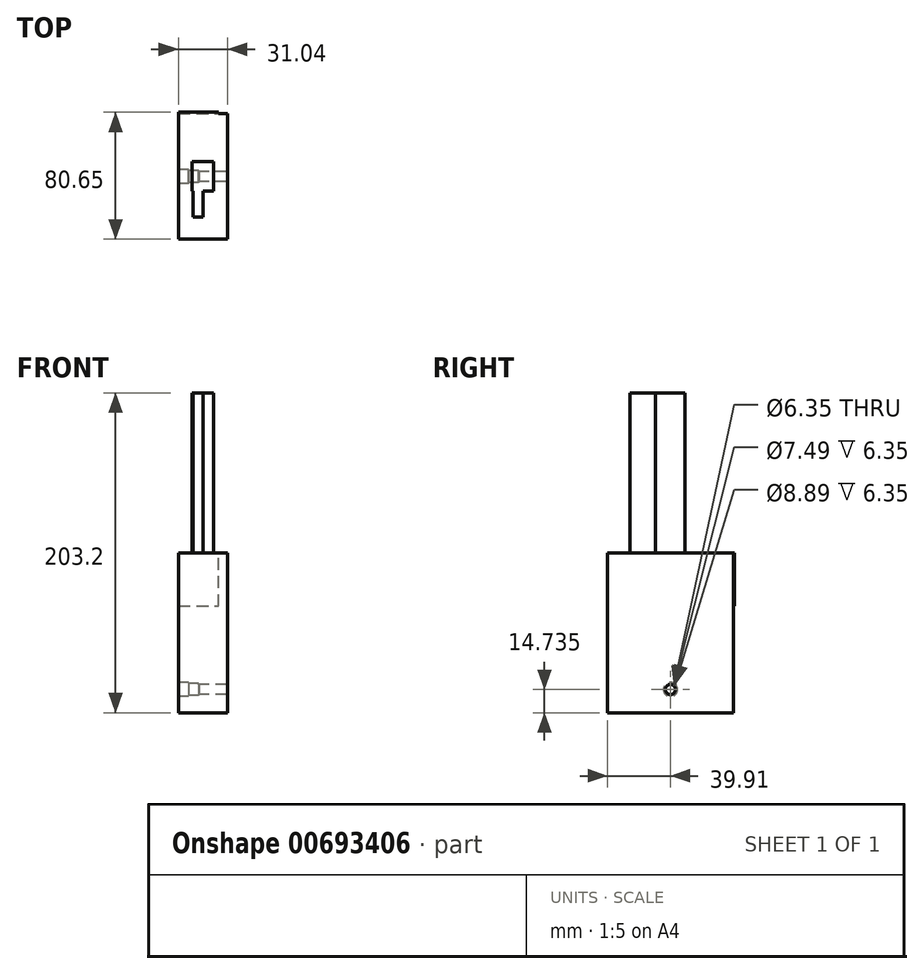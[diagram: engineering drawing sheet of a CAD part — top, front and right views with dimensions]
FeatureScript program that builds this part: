
annotation { "Feature Type Name" : "Feature", "Feature Type Description" : "" }
export const myFeature = defineFeature(function(context is Context, id is Id, definition is map)
    precondition{}
    {
        {
            var Q0;
            Q0=qCreatedBy(makeId("Top.planeOp"),FACE);
            var sketch = newSketch(context, id + "F0", { "sketchPlane" : qUnion([Q0])});
            skLineSegment(sketch, "E0.bottom", {"start": v(-15.52, 39.91) * mm, "end": v(15.52, 39.91) * mm});
            skLineSegment(sketch, "E0.top", {"start": v(-15.52, -39.91) * mm, "end": v(15.52, -39.91) * mm});
            skLineSegment(sketch, "E0.left", {"start": v(-15.52, 39.91) * mm, "end": v(-15.52, -39.91) * mm});
            skLineSegment(sketch, "E0.right", {"start": v(15.52, 39.91) * mm, "end": v(15.52, -39.91) * mm});
            skPoint(sketch, "E0.middle", {"position": v(0, 0) * mm});
            skSolve(sketch);
        }
        {
            var Q0;
            Q0=makeQuery(id+"F0.imprint","IMPRINT",FACE,{"disambiguationData":[TD([[makeQuery(id+"F0.imprint","IMPRINT",EDGE,{"derivedFrom":sQuery(id+"F0.wireOp",EDGE,"E0.bottom")}),-1.0]])]});
            extrude(context, id + "F1", {"entities" : qUnion([Q0]), "depth" : 101.6 * mm, "offsetDistance" : 25.4 * mm});
        }
        {
            var Q0;
            Q0=makeQuery(id+"F1.opExtrude","SWEPT_FACE",FACE,{"disambiguationData":[OSD([sQuery(id+"F0.wireOp",EDGE,"E0.left")])]});
            var sketch = newSketch(context, id + "F2", { "sketchPlane" : qUnion([Q0])});
            skPoint(sketch, "E1", {"position": v(0, 14.73) * mm});
            skSolve(sketch);
        }
        {
            var Q0;
            Q0=sQuery(id+"F2.wireOp",VERTEX,"E1");
            var Q1;
            Q1=makeQuery(id+"F1.opExtrude","SWEPT_BODY",BODY,{"disambiguationData":[OSD([sQuery(id+"F0.wireOp",EDGE,"E0.bottom"),sQuery(id+"F0.wireOp",EDGE,"E0.top"),sQuery(id+"F0.wireOp",EDGE,"E0.left"),sQuery(id+"F0.wireOp",EDGE,"E0.right")])]});
            hole(context, id + "F3", {"style" : HoleStyle.SIMPLE, "endStyle" : HoleEndStyle.THROUGH, "holeDiameter" : 6.35 * mm, "majorDiameter" : 6.35 * mm, "isTappedThrough" : true, "tappedDepth" : 12.7 * mm, "tapClearance" : 3, "locations" : qUnion([Q0]), "scope" : qUnion([Q1])});
        }
        {
            var Q0;
            Q0=makeQuery(id+"F1.opExtrude","SWEPT_FACE",FACE,{"disambiguationData":[OSD([sQuery(id+"F0.wireOp",EDGE,"E0.left")])]});
            var sketch = newSketch(context, id + "F4", { "sketchPlane" : qUnion([Q0])});
            skCircle(sketch, "E2", {"center": v(0, 14.73) * mm, "radius": 5.53 * mm});
            skSolve(sketch);
        }
        {
            var Q0;
            Q0=sQuery(id+"F4.wireOp",VERTEX,"E2.center");
            var Q1;
            Q1=makeQuery(id+"F1.opExtrude","SWEPT_BODY",BODY,{"disambiguationData":[OSD([sQuery(id+"F0.wireOp",EDGE,"E0.bottom"),sQuery(id+"F0.wireOp",EDGE,"E0.top"),sQuery(id+"F0.wireOp",EDGE,"E0.left"),sQuery(id+"F0.wireOp",EDGE,"E0.right")])]});
            hole(context, id + "F5", {"style" : HoleStyle.C_BORE, "endStyle" : HoleEndStyle.BLIND, "holeDiameter" : 7.5 * mm, "cBoreDiameter" : 8.9 * mm, "cBoreDepth" : 6.35 * mm, "majorDiameter" : 6.35 * mm, "holeDepth" : 12.7 * mm, "isTappedThrough" : true, "tappedDepth" : 12.7 * mm, "tapClearance" : 3, "locations" : qUnion([Q0]), "scope" : qUnion([Q1])});
        }
        {
            var Q0;
            Q0=makeQuery(id+"F1.opExtrude","SWEPT_FACE",FACE,{"disambiguationData":[OSD([sQuery(id+"F0.wireOp",EDGE,"E0.left")])]});
            var sketch = newSketch(context, id + "F6", { "sketchPlane" : qUnion([Q0])});
            skLineSegment(sketch, "E3.bottom", {"start": v(6.59, 101.6) * mm, "end": v(-40.74, 101.6) * mm});
            skLineSegment(sketch, "E3.top", {"start": v(6.59, 67.7) * mm, "end": v(-40.74, 67.7) * mm});
            skLineSegment(sketch, "E3.left", {"start": v(6.59, 101.6) * mm, "end": v(6.59, 67.7) * mm});
            skLineSegment(sketch, "E3.right", {"start": v(-40.74, 101.6) * mm, "end": v(-40.74, 67.7) * mm});
            skPoint(sketch, "E3.middle", {"position": v(-17.08, 84.65) * mm});
            skLineSegment(sketch, "E4.bottom", {"start": v(0, 84.65) * mm, "end": v(-34.15, 84.65) * mm});
            skLineSegment(sketch, "E4.top", {"start": v(0, 84.65) * mm, "end": v(-34.15, 84.65) * mm});
            skLineSegment(sketch, "E4.left", {"start": v(0, 84.65) * mm, "end": v(0, 84.65) * mm});
            skLineSegment(sketch, "E4.right", {"start": v(-34.15, 84.65) * mm, "end": v(-34.15, 84.65) * mm});
            skSolve(sketch);
        }
        {
            var Q0;
            Q0 = qSketchRegion(id + "F6", true);
            extrude(context, id + "F7", {"entities" : qUnion([Q0]), "operationType" : NewBodyOperationType.ADD, "oppositeDirection" : true, "depth" : 25.4 * mm, "offsetDistance" : 25.4 * mm});
        }
        {
            var Q0;
            Q0=makeQuery(id+"F7.boolean.opBoolean","MERGE",FACE,{"derivedFrom":[makeQuery(id+"F1.opExtrude","CAP_FACE",FACE,{"disambiguationData":[OSD([sQuery(id+"F0.wireOp",EDGE,"E0.bottom"),sQuery(id+"F0.wireOp",EDGE,"E0.top"),sQuery(id+"F0.wireOp",EDGE,"E0.left"),sQuery(id+"F0.wireOp",EDGE,"E0.right")])],"isStart":false}),makeQuery(id+"F7.opExtrude","SWEPT_FACE",FACE,{"disambiguationData":[OSD([sQuery(id+"F6.wireOp",EDGE,"E3.bottom")])]})]});
            var sketch = newSketch(context, id + "F8", { "sketchPlane" : qUnion([Q0])});
            skLineSegment(sketch, "E5.bottom", {"start": v(-6.83, -9.36) * mm, "end": v(6.83, -9.36) * mm});
            skLineSegment(sketch, "E5.top", {"start": v(-6.83, 9.36) * mm, "end": v(6.83, 9.36) * mm});
            skLineSegment(sketch, "E5.left", {"start": v(-6.83, -9.36) * mm, "end": v(-6.83, 9.36) * mm});
            skLineSegment(sketch, "E5.right", {"start": v(6.83, -9.36) * mm, "end": v(6.83, 9.36) * mm});
            skPoint(sketch, "E5.middle", {"position": v(0, 0) * mm});
            skLineSegment(sketch, "E6.bottom", {"start": v(0, 0) * mm, "end": v(-6.21, 0) * mm});
            skLineSegment(sketch, "E6.top", {"start": v(0, -25.67) * mm, "end": v(-6.21, -25.67) * mm});
            skLineSegment(sketch, "E6.left", {"start": v(0, 0) * mm, "end": v(0, -25.67) * mm});
            skLineSegment(sketch, "E6.right", {"start": v(-6.21, 0) * mm, "end": v(-6.21, -25.67) * mm});
            skPoint(sketch, "E6.middle", {"position": v(-3.1, -12.84) * mm});
            skSolve(sketch);
        }
        {
            var Q0;
            {var subQ5=sQuery(id+"F8.wireOp",EDGE,"E6.top");Q0=makeQuery(id+"F8.imprint","IMPRINT",FACE,{"disambiguationData":[TD([[makeQuery(id+"F8.imprint","IMPRINT",EDGE,{"derivedFrom":subQ5}),-1.0]])]});}
            var Q1;
            Q1 = qSketchRegion(id + "F8", true);
            var Q2;
            {var subQ5=sQuery(id+"F8.wireOp",EDGE,"E6.bottom");Q2=makeQuery(id+"F8.imprint","IMPRINT",FACE,{"disambiguationData":[TD([[makeQuery(id+"F8.imprint","IMPRINT",EDGE,{"derivedFrom":subQ5}),1.0]])]});}
            extrude(context, id + "F9", {"entities" : qUnion([Q0, Q1, Q2]), "operationType" : NewBodyOperationType.ADD, "depth" : 101.6 * mm, "offsetDistance" : 25.4 * mm});
        }
    });
